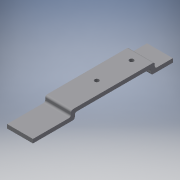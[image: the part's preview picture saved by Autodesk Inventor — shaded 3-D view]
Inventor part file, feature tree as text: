
AUTODESK INVENTOR PART (.ipt)
format: ipt  version: 2016 (Build 200138000, 138)  size: 156,672 bytes
history: native  units: mm
features: reference x9, extrude x5, sketch x5, fillet x1
ambient origin geometry x8: Origin, YZ Plane, XZ Plane, XY Plane, X Axis, Y Axis, Z Axis, Center Point
bodies: Solid1 (feature_tree)
feature tree (20):
  extrude  "Extrusion1"  Depth=130.0mm
  extrude  "Extrusion2"  Depth=6.0mm TaperAngle=0.0deg
  extrude  "Extrusion3"  Depth=6.0mm
  extrude  "Extrusion4"  Depth=34.0mm
  fillet  "Fillet1"  Radius=65.0mm
  extrude  "Extrusion5"  Depth=40.0mm
  sketch  "Sketch1"  dims[d0=40.0mm d1=130.0mm]
  sketch  "Sketch2"  dims[d2=6.0mm d3=0.0mm d4=6.0mm d5=0.0mm]
  reference  "Reference1"
  reference  "Reference2"
  sketch  "Sketch3"  dims[d6=6.0mm d7=6.0mm]
  sketch  "Sketch4"  dims[d8=3.0mm d9=0.0mm d10=34.0mm d11=65.0mm]
  sketch  "Sketch5"  dims[d12=40.0mm d13=40.0mm d14=6.0mm d15=0.0mm d16=3.0mm d17=8.0mm d18=6.0mm d19=0.0mm]
  reference  "Reference3"
  reference  "Reference4"
  reference  "Reference5"
  reference  "Reference6"
  reference  "Reference7"
  reference  "Reference8"
  reference  "Reference9"
